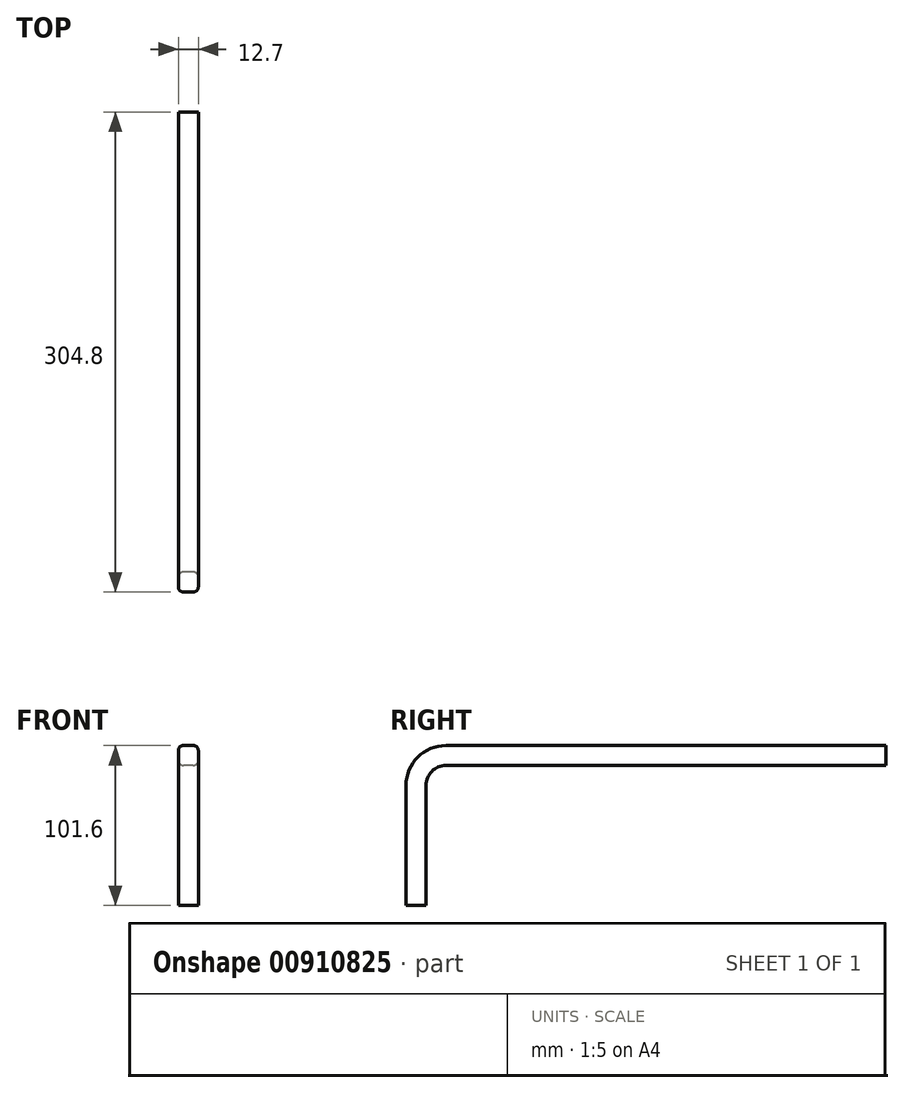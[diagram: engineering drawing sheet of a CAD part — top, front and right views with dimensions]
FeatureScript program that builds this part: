
annotation { "Feature Type Name" : "Feature", "Feature Type Description" : "" }
export const myFeature = defineFeature(function(context is Context, id is Id, definition is map)
    precondition{}
    {
        {
            var Q0;
            Q0=qCreatedBy(makeId("Right.planeOp"),FACE);
            var sketch = newSketch(context, id + "F0", { "sketchPlane" : qUnion([Q0])});
            skLineSegment(sketch, "E0", {"start": v(0, 0) * mm, "end": v(0, 76.2) * mm});
            skLineSegment(sketch, "E1", {"start": v(25.4, 101.6) * mm, "end": v(304.8, 101.6) * mm});
            skPoint(sketch, "E2.visualSharp", {"position": v(0, 101.6) * mm});
            skArc(sketch, "E2.filletArc", {"start": v(25.4, 101.6) * mm, "mid": v(7.44, 94.16) * mm, "end": v(0, 76.2) * mm});
            skArc(sketch, "E3.0", {"start": v(25.4, 88.9) * mm, "mid": v(16.42, 85.18) * mm, "end": v(12.7, 76.2) * mm});
            skLineSegment(sketch, "E3.1", {"start": v(12.7, 0) * mm, "end": v(12.7, 76.2) * mm});
            skLineSegment(sketch, "E4.0", {"start": v(25.4, 88.9) * mm, "end": v(304.8, 88.9) * mm});
            skLineSegment(sketch, "E5", {"start": v(0, 0) * mm, "end": v(12.7, 0) * mm});
            skLineSegment(sketch, "E6", {"start": v(304.8, 88.9) * mm, "end": v(304.8, 101.6) * mm});
            skSolve(sketch);
        }
        {
            var Q0;
            Q0 = qSketchRegion(id + "F0", true);
            extrude(context, id + "F1", {"entities" : qUnion([Q0]), "depth" : 12.7 * mm, "offsetDistance" : 25.4 * mm});
        }
        {
            var Q0;
            Q0=makeQuery(id+"F1.opExtrude","CAP_EDGE",EDGE,{"disambiguationData":[OSD([sQuery(id+"F0.wireOp",EDGE,"E2.filletArc")])],"isStart":false});
            var Q1;
            Q1=makeQuery(id+"F1.opExtrude","CAP_EDGE",EDGE,{"disambiguationData":[OSD([sQuery(id+"F0.wireOp",EDGE,"E4.0")])],"isStart":false});
            var Q2;
            Q2=makeQuery(id+"F1.opExtrude","CAP_EDGE",EDGE,{"disambiguationData":[OSD([sQuery(id+"F0.wireOp",EDGE,"E1")])],"isStart":true});
            var Q3;
            Q3=makeQuery(id+"F1.opExtrude","CAP_EDGE",EDGE,{"disambiguationData":[OSD([sQuery(id+"F0.wireOp",EDGE,"E4.0")])],"isStart":true});
            fillet(context, id + "F2", {"entities" : qUnion([Q0, Q1, Q2, Q3]), "radius" : 3.17 * mm, "tangentPropagation" : true, "allowEdgeOverflow" : false});
        }
    });
